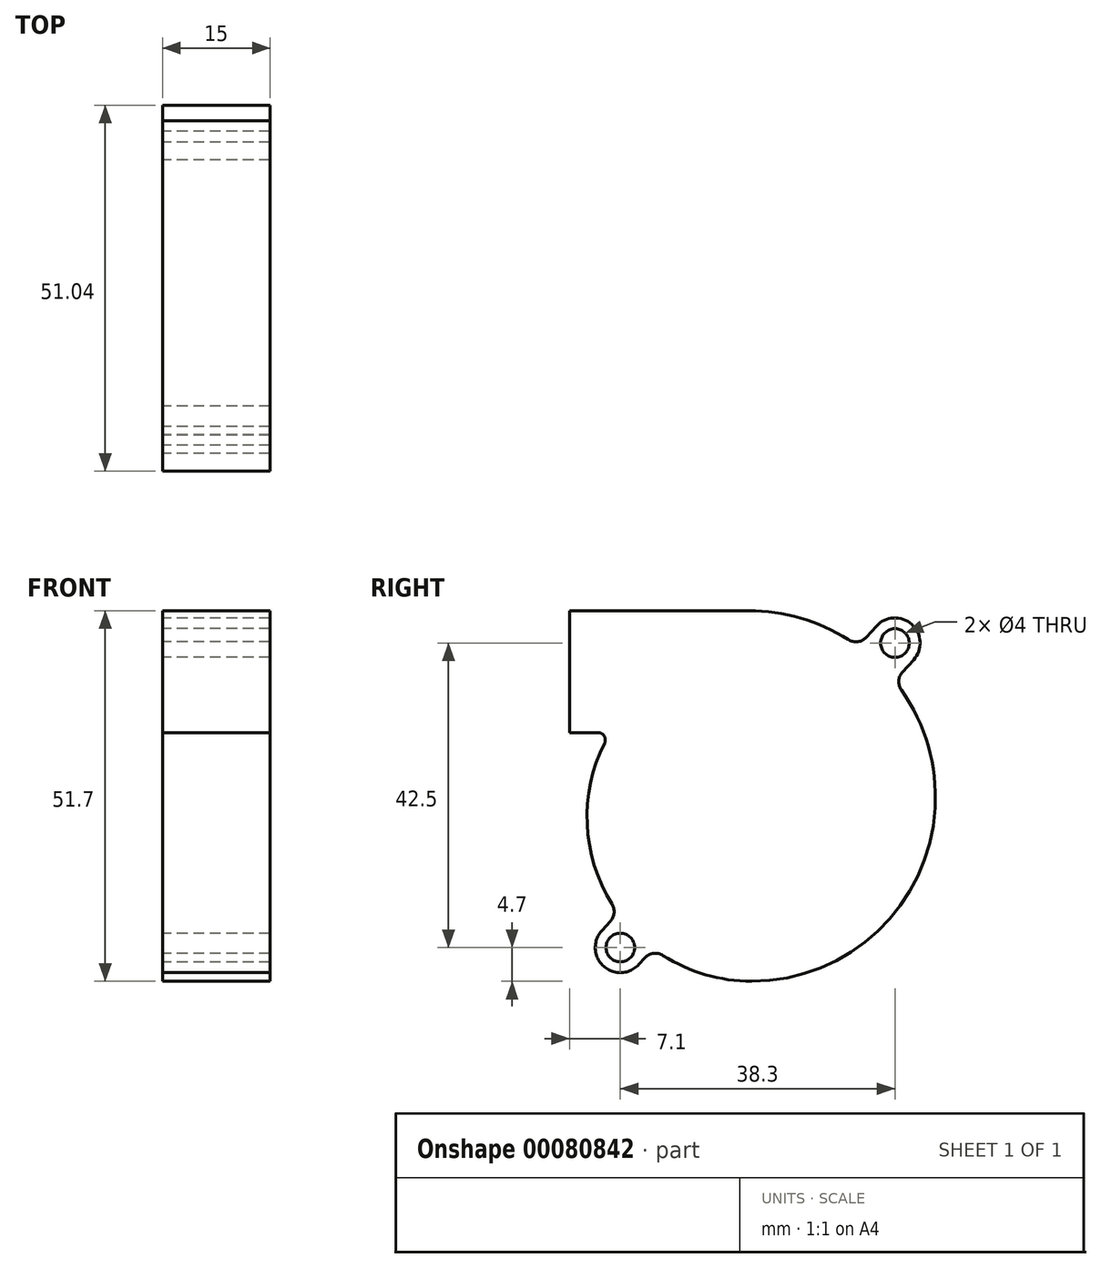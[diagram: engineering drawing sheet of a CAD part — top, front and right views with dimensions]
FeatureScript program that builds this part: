
annotation { "Feature Type Name" : "Feature", "Feature Type Description" : "" }
export const myFeature = defineFeature(function(context is Context, id is Id, definition is map)
    precondition{}
    {
        {
            var Q0;
            Q0=qCreatedBy(makeId("Right.planeOp"),FACE);
            var sketch = newSketch(context, id + "F0", { "sketchPlane" : qUnion([Q0])});
            skCircle(sketch, "E0", {"center": v(0, 0) * mm, "radius": 12 * mm});
            skCircle(sketch, "E1", {"center": v(20, 23) * mm, "radius": 2 * mm});
            skCircle(sketch, "E2", {"center": v(-18.3, -19.5) * mm, "radius": 2 * mm});
            skLineSegment(sketch, "E3", {"start": v(-25.4, 27.5) * mm, "end": v(-25.4, 10.5) * mm});
            skLineSegment(sketch, "E4", {"start": v(25.6, 45.37) * mm, "end": v(25.6, -37.89) * mm, "construction": true});
            skCircle(sketch, "E5", {"center": v(0, 0) * mm, "radius": 16 * mm});
            skLineSegment(sketch, "E6", {"start": v(-25.4, 27.5) * mm, "end": v(64.88, 27.5) * mm, "construction": true});
            skLineSegment(sketch, "E7", {"start": v(-25.4, 27.5) * mm, "end": v(-0.4, 27.5) * mm});
            skArc(sketch, "E8", {"start": v(22.6, 20.66) * mm, "mid": v(22.34, 25.6) * mm, "end": v(17.4, 25.34) * mm});
            skArc(sketch, "E9", {"start": v(-20.9, -17.16) * mm, "mid": v(-20.64, -22.1) * mm, "end": v(-15.7, -21.84) * mm});
            skArc(sketch, "E10", {"start": v(25.6, 0) * mm, "mid": v(24.64, 8.62) * mm, "end": v(20.9, 16.44) * mm});
            skArc(sketch, "E11", {"start": v(0, -24.2) * mm, "mid": v(17.62, -17.2) * mm, "end": v(25.6, 0) * mm});
            skArc(sketch, "E12", {"start": v(-20.5, 9.05) * mm, "mid": v(-22.93, -2.31) * mm, "end": v(-19.47, -13.4) * mm});
            skLineSegment(sketch, "E13", {"start": v(-25.4, 10.5) * mm, "end": v(-21.4, 10.5) * mm});
            skPoint(sketch, "E14.visualSharp", {"position": v(-19.71, 10.5) * mm});
            skArc(sketch, "E14.filletArc", {"start": v(-20.5, 9.05) * mm, "mid": v(-20.55, 10.02) * mm, "end": v(-21.4, 10.5) * mm});
            skLineSegment(sketch, "E15", {"start": v(-20.9, -17.16) * mm, "end": v(-19.68, -15.8) * mm});
            skLineSegment(sketch, "E16", {"start": v(-15.7, -21.84) * mm, "end": v(-14.9, -20.95) * mm});
            skLineSegment(sketch, "E17", {"start": v(17.4, 25.34) * mm, "end": v(16.04, 23.84) * mm});
            skLineSegment(sketch, "E18", {"start": v(22.6, 20.66) * mm, "end": v(21.05, 18.93) * mm});
            skArc(sketch, "E19.trimOffspring", {"start": v(-12.34, -20.6) * mm, "mid": v(-6.43, -23.29) * mm, "end": v(0, -24.2) * mm});
            skArc(sketch, "E20.trimOffspring", {"start": v(13.5, 23.49) * mm, "mid": v(6.83, 26.48) * mm, "end": v(-0.4, 27.5) * mm});
            skPoint(sketch, "E21.visualSharp", {"position": v(14.88, 22.55) * mm});
            skArc(sketch, "E21.filletArc", {"start": v(13.5, 23.49) * mm, "mid": v(14.83, 23.2) * mm, "end": v(16.04, 23.84) * mm});
            skPoint(sketch, "E22.visualSharp", {"position": v(19.95, 17.71) * mm});
            skArc(sketch, "E22.filletArc", {"start": v(21.05, 18.93) * mm, "mid": v(20.54, 17.72) * mm, "end": v(20.9, 16.44) * mm});
            skPoint(sketch, "E23.visualSharp", {"position": v(-18.64, -14.65) * mm});
            skArc(sketch, "E23.filletArc", {"start": v(-19.68, -15.8) * mm, "mid": v(-19.17, -14.64) * mm, "end": v(-19.47, -13.4) * mm});
            skPoint(sketch, "E24.visualSharp", {"position": v(-13.72, -19.65) * mm});
            skArc(sketch, "E24.filletArc", {"start": v(-12.34, -20.6) * mm, "mid": v(-13.68, -20.31) * mm, "end": v(-14.9, -20.95) * mm});
            skSolve(sketch);
        }
        {
            var Q0;
            Q0=makeQuery(id+"F0.imprint","IMPRINT",FACE,{"disambiguationData":[TD([[makeQuery(id+"F0.imprint","IMPRINT",EDGE,{"derivedFrom":sQuery(id+"F0.wireOp",EDGE,"E1")}),-1.0]])]});
            var Q1;
            Q1=makeQuery(id+"F0.imprint","IMPRINT",FACE,{"disambiguationData":[TD([[makeQuery(id+"F0.imprint","IMPRINT",EDGE,{"derivedFrom":sQuery(id+"F0.wireOp",EDGE,"E0")}),-1.0]])]});
            var Q2;
            Q2=makeQuery(id+"F0.imprint","IMPRINT",FACE,{"disambiguationData":[TD([[makeQuery(id+"F0.imprint","IMPRINT",EDGE,{"derivedFrom":sQuery(id+"F0.wireOp",EDGE,"E0")}),1.0]])]});
            extrude(context, id + "F1", {"entities" : qUnion([Q0, Q1, Q2]), "depth" : 15 * mm});
        }
    });
